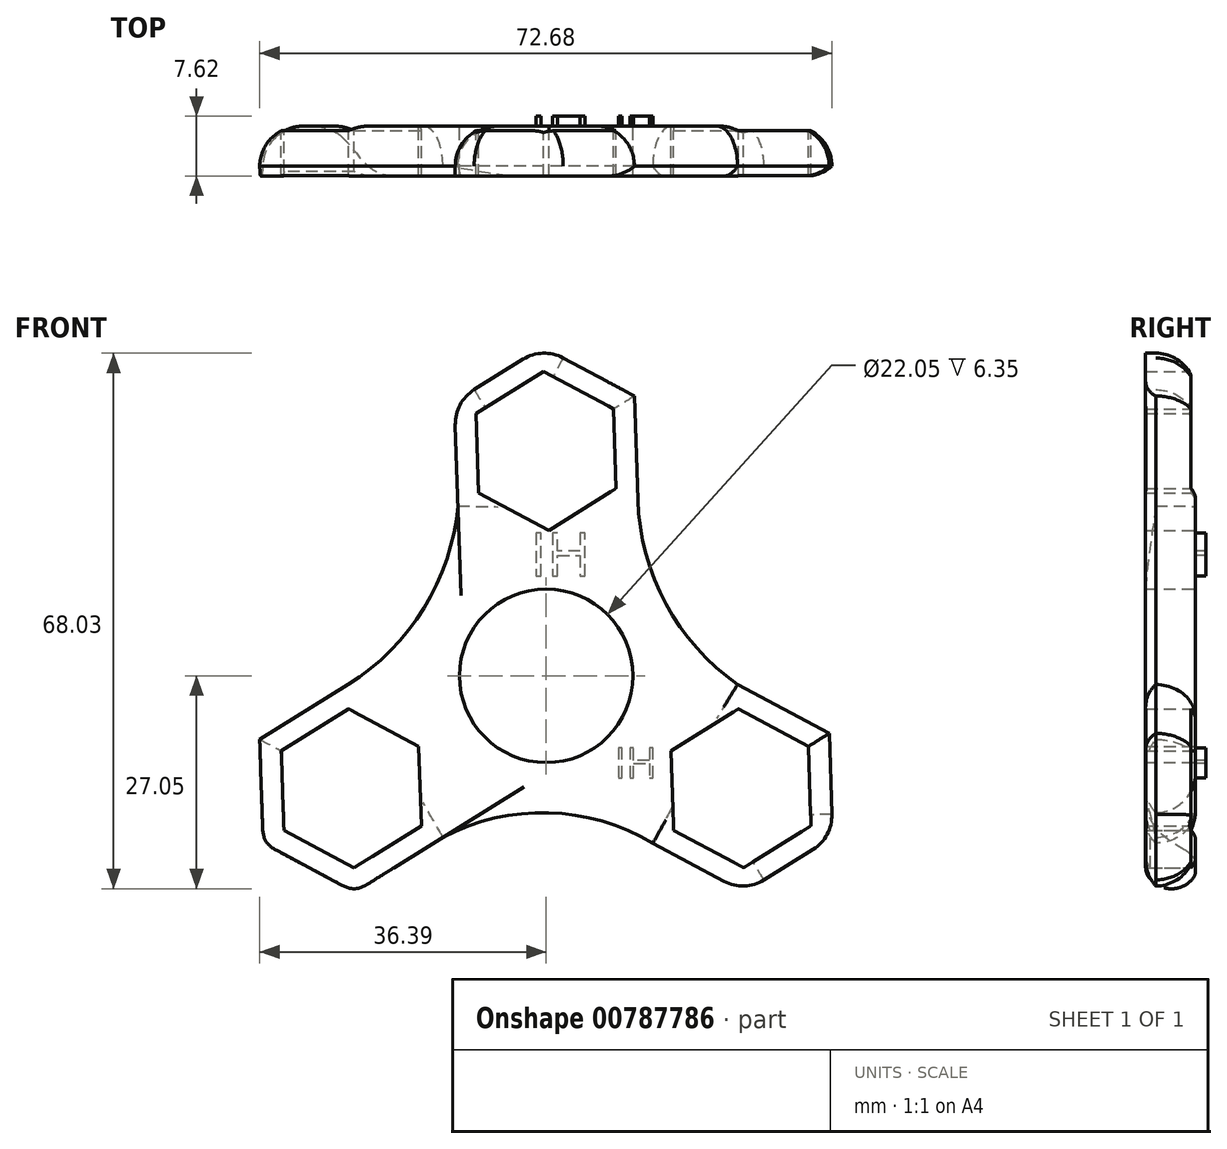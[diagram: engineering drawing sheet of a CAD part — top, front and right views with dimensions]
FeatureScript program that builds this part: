
annotation { "Feature Type Name" : "Feature", "Feature Type Description" : "" }
export const myFeature = defineFeature(function(context is Context, id is Id, definition is map)
    precondition{}
    {
        {
            var Q0;
            Q0=qCreatedBy(makeId("Front.planeOp"),FACE);
            var sketch = newSketch(context, id + "F0", { "sketchPlane" : qUnion([Q0])});
            skCircle(sketch, "E0", {"center": v(0, 0) * mm, "radius": 11.02 * mm});
            skCircle(sketch, "E1", {"center": v(0, 0) * mm, "radius": 14.29 * mm});
            skCircle(sketch, "E2", {"center": v(0, 28.58) * mm, "radius": 8.74 * mm});
            skCircle(sketch, "E3", {"center": v(0, 28.58) * mm, "radius": 11.43 * mm});
            skCircle(sketch, "E4.cCircle", {"center": v(0, 28.58) * mm, "radius": 8.74 * mm, "construction": true});
            skLineSegment(sketch, "E4.0", {"start": v(0.33, 18.5) * mm, "end": v(-8.57, 23.25) * mm});
            skLineSegment(sketch, "E4.1", {"start": v(-8.57, 23.25) * mm, "end": v(-8.9, 33.33) * mm});
            skLineSegment(sketch, "E4.2", {"start": v(-8.9, 33.33) * mm, "end": v(-0.33, 38.66) * mm});
            skLineSegment(sketch, "E4.3", {"start": v(-0.33, 38.66) * mm, "end": v(8.57, 33.9) * mm});
            skLineSegment(sketch, "E4.4", {"start": v(8.57, 33.9) * mm, "end": v(8.9, 23.82) * mm});
            skLineSegment(sketch, "E4.5", {"start": v(8.9, 23.82) * mm, "end": v(0.33, 18.5) * mm});
            skPoint(sketch, "E4.0.midPoint", {"position": v(-4.12, 20.87) * mm});
            skCircle(sketch, "E5.cCircle", {"center": v(0, 28.58) * mm, "radius": 11.43 * mm, "construction": true});
            skLineSegment(sketch, "E5.0", {"start": v(0.43, 15.38) * mm, "end": v(-11.2, 21.6) * mm});
            skLineSegment(sketch, "E5.1", {"start": v(-11.2, 21.6) * mm, "end": v(-11.64, 34.8) * mm});
            skLineSegment(sketch, "E5.2", {"start": v(-11.64, 34.8) * mm, "end": v(-0.43, 41.77) * mm});
            skLineSegment(sketch, "E5.3", {"start": v(-0.43, 41.77) * mm, "end": v(11.2, 35.55) * mm});
            skLineSegment(sketch, "E5.4", {"start": v(11.2, 35.55) * mm, "end": v(11.64, 22.36) * mm});
            skLineSegment(sketch, "E5.5", {"start": v(11.64, 22.36) * mm, "end": v(0.43, 15.38) * mm});
            skPoint(sketch, "E5.0.midPoint", {"position": v(-5.39, 18.5) * mm});
            skCircle(sketch, "E6.1.0", {"center": v(-24.75, -14.29) * mm, "radius": 8.74 * mm, "construction": true});
            skPoint(sketch, "E6.1.1", {"position": v(-16.01, -14) * mm});
            skPoint(sketch, "E6.1.2", {"position": v(-13.32, -13.91) * mm});
            skLineSegment(sketch, "E6.1.3", {"start": v(-35.95, -21.26) * mm, "end": v(-36.39, -8.07) * mm});
            skLineSegment(sketch, "E6.1.4", {"start": v(-24.31, -27.48) * mm, "end": v(-35.95, -21.26) * mm});
            skLineSegment(sketch, "E6.1.5", {"start": v(-13.1, -20.5) * mm, "end": v(-24.31, -27.48) * mm});
            skLineSegment(sketch, "E6.1.6", {"start": v(-25.18, -1.1) * mm, "end": v(-13.54, -7.32) * mm});
            skLineSegment(sketch, "E6.1.7", {"start": v(-15.85, -19.04) * mm, "end": v(-24.42, -24.37) * mm});
            skLineSegment(sketch, "E6.1.8", {"start": v(-24.42, -24.37) * mm, "end": v(-33.31, -19.62) * mm});
            skLineSegment(sketch, "E6.1.9", {"start": v(-33.65, -9.53) * mm, "end": v(-25.08, -4.2) * mm});
            skLineSegment(sketch, "E6.1.10", {"start": v(-25.08, -4.2) * mm, "end": v(-16.18, -8.96) * mm});
            skCircle(sketch, "E6.1.11", {"center": v(-24.75, -14.29) * mm, "radius": 11.43 * mm, "construction": true});
            skLineSegment(sketch, "E6.1.12", {"start": v(-36.39, -8.07) * mm, "end": v(-25.18, -1.1) * mm});
            skCircle(sketch, "E6.1.13", {"center": v(-24.75, -14.29) * mm, "radius": 8.74 * mm});
            skCircle(sketch, "E6.1.14", {"center": v(-24.75, -14.29) * mm, "radius": 11.43 * mm});
            skLineSegment(sketch, "E6.1.15", {"start": v(-16.18, -8.96) * mm, "end": v(-15.85, -19.04) * mm});
            skLineSegment(sketch, "E6.1.16", {"start": v(-33.31, -19.62) * mm, "end": v(-33.65, -9.53) * mm});
            skLineSegment(sketch, "E6.1.17", {"start": v(-13.54, -7.32) * mm, "end": v(-13.1, -20.5) * mm});
            skCircle(sketch, "E6.2.0", {"center": v(24.75, -14.29) * mm, "radius": 8.74 * mm, "construction": true});
            skPoint(sketch, "E6.2.1", {"position": v(20.13, -6.87) * mm});
            skPoint(sketch, "E6.2.2", {"position": v(18.7, -4.58) * mm});
            skLineSegment(sketch, "E6.2.3", {"start": v(36.39, -20.5) * mm, "end": v(25.18, -27.48) * mm});
            skLineSegment(sketch, "E6.2.4", {"start": v(35.95, -7.32) * mm, "end": v(36.39, -20.5) * mm});
            skLineSegment(sketch, "E6.2.5", {"start": v(24.31, -1.1) * mm, "end": v(35.95, -7.32) * mm});
            skLineSegment(sketch, "E6.2.6", {"start": v(13.54, -21.26) * mm, "end": v(13.1, -8.07) * mm});
            skLineSegment(sketch, "E6.2.7", {"start": v(24.42, -4.2) * mm, "end": v(33.31, -8.96) * mm});
            skLineSegment(sketch, "E6.2.8", {"start": v(33.31, -8.96) * mm, "end": v(33.65, -19.04) * mm});
            skLineSegment(sketch, "E6.2.9", {"start": v(25.08, -24.37) * mm, "end": v(16.18, -19.62) * mm});
            skLineSegment(sketch, "E6.2.10", {"start": v(16.18, -19.62) * mm, "end": v(15.85, -9.53) * mm});
            skCircle(sketch, "E6.2.11", {"center": v(24.75, -14.29) * mm, "radius": 11.43 * mm, "construction": true});
            skLineSegment(sketch, "E6.2.12", {"start": v(25.18, -27.48) * mm, "end": v(13.54, -21.26) * mm});
            skCircle(sketch, "E6.2.13", {"center": v(24.75, -14.29) * mm, "radius": 8.74 * mm});
            skCircle(sketch, "E6.2.14", {"center": v(24.75, -14.29) * mm, "radius": 11.43 * mm});
            skLineSegment(sketch, "E6.2.15", {"start": v(15.85, -9.53) * mm, "end": v(24.42, -4.2) * mm});
            skLineSegment(sketch, "E6.2.16", {"start": v(33.65, -19.04) * mm, "end": v(25.08, -24.37) * mm});
            skLineSegment(sketch, "E6.2.17", {"start": v(13.1, -8.07) * mm, "end": v(24.31, -1.1) * mm});
            skArc(sketch, "E7", {"start": v(-25.18, -1.1) * mm, "mid": v(-15.52, 8.6) * mm, "end": v(-11.2, 21.6) * mm});
            skArc(sketch, "E8", {"start": v(11.64, 22.36) * mm, "mid": v(15.22, 9.14) * mm, "end": v(24.31, -1.1) * mm});
            skArc(sketch, "E9", {"start": v(13.54, -21.26) * mm, "mid": v(0.32, -17.4) * mm, "end": v(-13.1, -20.5) * mm});
            skSolve(sketch);
        }
        {
            var Q0;
            {var subQ0=sQuery(id+"F0.wireOp",EDGE,"E5.2");var subQ1=sQuery(id+"F0.wireOp",EDGE,"E3");var subQ2=makeQuery(id+"F0.imprint","INTERSECT",VERTEX,{"derivedFrom":[subQ1,subQ0]});Q0=makeQuery(id+"F0.imprint","IMPRINT",FACE,{"disambiguationData":[TD([[makeQuery(id+"F0.imprint","IMPRINT",EDGE,{"disambiguationData":[TD([[subQ2,-1.0]])],"derivedFrom":subQ1}),-1.0]])]});}
            var Q1;
            {var subQ0=sQuery(id+"F0.wireOp",EDGE,"E5.3");var subQ1=sQuery(id+"F0.wireOp",EDGE,"E3");var subQ2=makeQuery(id+"F0.imprint","INTERSECT",VERTEX,{"derivedFrom":[subQ1,subQ0]});Q1=makeQuery(id+"F0.imprint","IMPRINT",FACE,{"disambiguationData":[TD([[makeQuery(id+"F0.imprint","IMPRINT",EDGE,{"disambiguationData":[TD([[subQ2,-1.0]])],"derivedFrom":subQ1}),-1.0]])]});}
            var Q2;
            {var subQ10=sQuery(id+"F0.wireOp",EDGE,"E3");var subQ14=makeQuery(id+"F0.imprint","INTERSECT",VERTEX,{"derivedFrom":[subQ10,sQuery(id+"F0.wireOp",EDGE,"E5.3")]});Q2=makeQuery(id+"F0.imprint","IMPRINT",FACE,{"disambiguationData":[TD([[makeQuery(id+"F0.imprint","IMPRINT",EDGE,{"disambiguationData":[TD([[subQ14,1.0]])],"derivedFrom":subQ10}),1.0]])]});}
            var Q3;
            {var subQ0=sQuery(id+"F0.wireOp",EDGE,"E5.3");var subQ1=sQuery(id+"F0.wireOp",EDGE,"E3");var subQ2=makeQuery(id+"F0.imprint","INTERSECT",VERTEX,{"derivedFrom":[subQ1,subQ0]});Q3=makeQuery(id+"F0.imprint","IMPRINT",FACE,{"disambiguationData":[TD([[makeQuery(id+"F0.imprint","IMPRINT",EDGE,{"disambiguationData":[TD([[subQ2,1.0]])],"derivedFrom":subQ1}),-1.0]])]});}
            var Q4;
            {var subQ0=sQuery(id+"F0.wireOp",EDGE,"E5.4");var subQ1=sQuery(id+"F0.wireOp",EDGE,"E3");var subQ2=makeQuery(id+"F0.imprint","INTERSECT",VERTEX,{"derivedFrom":[subQ1,subQ0]});Q4=makeQuery(id+"F0.imprint","IMPRINT",FACE,{"disambiguationData":[TD([[makeQuery(id+"F0.imprint","IMPRINT",EDGE,{"disambiguationData":[TD([[subQ2,1.0]])],"derivedFrom":subQ1}),-1.0]])]});}
            var Q5;
            {var subQ0=sQuery(id+"F0.wireOp",EDGE,"E5.0");var subQ1=sQuery(id+"F0.wireOp",EDGE,"E3");var subQ2=makeQuery(id+"F0.imprint","INTERSECT",VERTEX,{"derivedFrom":[subQ1,subQ0]});Q5=makeQuery(id+"F0.imprint","IMPRINT",FACE,{"disambiguationData":[TD([[makeQuery(id+"F0.imprint","IMPRINT",EDGE,{"disambiguationData":[TD([[subQ2,-1.0]])],"derivedFrom":subQ1}),-1.0]])]});}
            var Q6;
            {var subQ0=sQuery(id+"F0.wireOp",EDGE,"E5.1");var subQ1=sQuery(id+"F0.wireOp",EDGE,"E3");var subQ2=makeQuery(id+"F0.imprint","INTERSECT",VERTEX,{"derivedFrom":[subQ1,subQ0]});Q6=makeQuery(id+"F0.imprint","IMPRINT",FACE,{"disambiguationData":[TD([[makeQuery(id+"F0.imprint","IMPRINT",EDGE,{"disambiguationData":[TD([[subQ2,-1.0]])],"derivedFrom":subQ1}),-1.0]])]});}
            var Q7;
            Q7=makeQuery(id+"F0.imprint","IMPRINT",FACE,{"disambiguationData":[TD([[makeQuery(id+"F0.imprint","IMPRINT",EDGE,{"derivedFrom":sQuery(id+"F0.wireOp",EDGE,"E1")}),-1.0]])]});
            var Q8;
            Q8=makeQuery(id+"F0.imprint","IMPRINT",FACE,{"disambiguationData":[TD([[makeQuery(id+"F0.imprint","IMPRINT",EDGE,{"derivedFrom":sQuery(id+"F0.wireOp",EDGE,"E0")}),-1.0]])]});
            var Q9;
            {var subQ1=sQuery(id+"F0.wireOp",EDGE,"E6.2.5");var subQ3=sQuery(id+"F0.wireOp",EDGE,"E6.2.14");var subQ4=makeQuery(id+"F0.imprint","INTERSECT",VERTEX,{"derivedFrom":[subQ1,subQ3]});Q9=makeQuery(id+"F0.imprint","IMPRINT",FACE,{"disambiguationData":[TD([[makeQuery(id+"F0.imprint","IMPRINT",EDGE,{"disambiguationData":[TD([[subQ4,-1.0]])],"derivedFrom":subQ3}),-1.0]])]});}
            var Q10;
            {var subQ1=sQuery(id+"F0.wireOp",EDGE,"E6.1.5");var subQ3=sQuery(id+"F0.wireOp",EDGE,"E6.1.14");var subQ4=makeQuery(id+"F0.imprint","INTERSECT",VERTEX,{"derivedFrom":[subQ1,subQ3]});Q10=makeQuery(id+"F0.imprint","IMPRINT",FACE,{"disambiguationData":[TD([[makeQuery(id+"F0.imprint","IMPRINT",EDGE,{"disambiguationData":[TD([[subQ4,-1.0]])],"derivedFrom":subQ3}),-1.0]])]});}
            var Q11;
            {var subQ0=sQuery(id+"F0.wireOp",EDGE,"E6.1.17");var subQ1=sQuery(id+"F0.wireOp",EDGE,"E6.1.6");var subQ2=makeQuery(id+"F0.imprint","INTERSECT",VERTEX,{"derivedFrom":[subQ1,subQ0]});Q11=makeQuery(id+"F0.imprint","IMPRINT",FACE,{"disambiguationData":[TD([[makeQuery(id+"F0.imprint","IMPRINT",EDGE,{"disambiguationData":[TD([[subQ2,1.0]])],"derivedFrom":subQ1}),-1.0]])]});}
            var Q12;
            {var subQ0=sQuery(id+"F0.wireOp",EDGE,"E6.1.12");var subQ3=sQuery(id+"F0.wireOp",EDGE,"E6.1.14");var subQ5=makeQuery(id+"F0.imprint","INTERSECT",VERTEX,{"derivedFrom":[subQ0,subQ3]});Q12=makeQuery(id+"F0.imprint","IMPRINT",FACE,{"disambiguationData":[TD([[makeQuery(id+"F0.imprint","IMPRINT",EDGE,{"disambiguationData":[TD([[subQ5,1.0]])],"derivedFrom":subQ3}),-1.0]])]});}
            var Q13;
            {var subQ0=sQuery(id+"F0.wireOp",EDGE,"E6.1.15");var subQ14=sQuery(id+"F0.wireOp",EDGE,"E6.1.7");var subQ15=makeQuery(id+"F0.imprint","INTERSECT",VERTEX,{"derivedFrom":[subQ14,subQ0]});Q13=makeQuery(id+"F0.imprint","IMPRINT",FACE,{"disambiguationData":[TD([[makeQuery(id+"F0.imprint","IMPRINT",EDGE,{"disambiguationData":[TD([[subQ15,-1.0]])],"derivedFrom":subQ14}),1.0]])]});}
            var Q14;
            {var subQ0=sQuery(id+"F0.wireOp",EDGE,"E6.1.12");var subQ1=sQuery(id+"F0.wireOp",EDGE,"E6.1.3");var subQ2=makeQuery(id+"F0.imprint","INTERSECT",VERTEX,{"derivedFrom":[subQ1,subQ0]});Q14=makeQuery(id+"F0.imprint","IMPRINT",FACE,{"disambiguationData":[TD([[makeQuery(id+"F0.imprint","IMPRINT",EDGE,{"disambiguationData":[TD([[subQ2,1.0]])],"derivedFrom":subQ1}),-1.0]])]});}
            var Q15;
            {var subQ0=sQuery(id+"F0.wireOp",EDGE,"E6.1.4");var subQ1=sQuery(id+"F0.wireOp",EDGE,"E6.1.3");var subQ2=makeQuery(id+"F0.imprint","INTERSECT",VERTEX,{"derivedFrom":[subQ1,subQ0]});Q15=makeQuery(id+"F0.imprint","IMPRINT",FACE,{"disambiguationData":[TD([[makeQuery(id+"F0.imprint","IMPRINT",EDGE,{"disambiguationData":[TD([[subQ2,-1.0]])],"derivedFrom":subQ1}),-1.0]])]});}
            var Q16;
            {var subQ0=sQuery(id+"F0.wireOp",EDGE,"E6.1.5");var subQ1=sQuery(id+"F0.wireOp",EDGE,"E6.1.4");var subQ2=makeQuery(id+"F0.imprint","INTERSECT",VERTEX,{"derivedFrom":[subQ1,subQ0]});Q16=makeQuery(id+"F0.imprint","IMPRINT",FACE,{"disambiguationData":[TD([[makeQuery(id+"F0.imprint","IMPRINT",EDGE,{"disambiguationData":[TD([[subQ2,-1.0]])],"derivedFrom":subQ1}),-1.0]])]});}
            var Q17;
            {var subQ0=sQuery(id+"F0.wireOp",EDGE,"E6.2.17");var subQ1=sQuery(id+"F0.wireOp",EDGE,"E6.2.6");var subQ2=makeQuery(id+"F0.imprint","INTERSECT",VERTEX,{"derivedFrom":[subQ1,subQ0]});Q17=makeQuery(id+"F0.imprint","IMPRINT",FACE,{"disambiguationData":[TD([[makeQuery(id+"F0.imprint","IMPRINT",EDGE,{"disambiguationData":[TD([[subQ2,1.0]])],"derivedFrom":subQ1}),-1.0]])]});}
            var Q18;
            {var subQ0=sQuery(id+"F0.wireOp",EDGE,"E6.2.12");var subQ3=sQuery(id+"F0.wireOp",EDGE,"E6.2.14");var subQ5=makeQuery(id+"F0.imprint","INTERSECT",VERTEX,{"derivedFrom":[subQ0,subQ3]});Q18=makeQuery(id+"F0.imprint","IMPRINT",FACE,{"disambiguationData":[TD([[makeQuery(id+"F0.imprint","IMPRINT",EDGE,{"disambiguationData":[TD([[subQ5,1.0]])],"derivedFrom":subQ3}),-1.0]])]});}
            var Q19;
            {var subQ0=sQuery(id+"F0.wireOp",EDGE,"E6.2.12");var subQ1=sQuery(id+"F0.wireOp",EDGE,"E6.2.3");var subQ2=makeQuery(id+"F0.imprint","INTERSECT",VERTEX,{"derivedFrom":[subQ1,subQ0]});Q19=makeQuery(id+"F0.imprint","IMPRINT",FACE,{"disambiguationData":[TD([[makeQuery(id+"F0.imprint","IMPRINT",EDGE,{"disambiguationData":[TD([[subQ2,1.0]])],"derivedFrom":subQ1}),-1.0]])]});}
            var Q20;
            {var subQ0=sQuery(id+"F0.wireOp",EDGE,"E6.2.4");var subQ1=sQuery(id+"F0.wireOp",EDGE,"E6.2.3");var subQ2=makeQuery(id+"F0.imprint","INTERSECT",VERTEX,{"derivedFrom":[subQ1,subQ0]});Q20=makeQuery(id+"F0.imprint","IMPRINT",FACE,{"disambiguationData":[TD([[makeQuery(id+"F0.imprint","IMPRINT",EDGE,{"disambiguationData":[TD([[subQ2,-1.0]])],"derivedFrom":subQ1}),-1.0]])]});}
            var Q21;
            {var subQ0=sQuery(id+"F0.wireOp",EDGE,"E6.2.5");var subQ1=sQuery(id+"F0.wireOp",EDGE,"E6.2.4");var subQ2=makeQuery(id+"F0.imprint","INTERSECT",VERTEX,{"derivedFrom":[subQ1,subQ0]});Q21=makeQuery(id+"F0.imprint","IMPRINT",FACE,{"disambiguationData":[TD([[makeQuery(id+"F0.imprint","IMPRINT",EDGE,{"disambiguationData":[TD([[subQ2,-1.0]])],"derivedFrom":subQ1}),-1.0]])]});}
            var Q22;
            {var subQ0=sQuery(id+"F0.wireOp",EDGE,"E6.2.15");var subQ14=sQuery(id+"F0.wireOp",EDGE,"E6.2.7");var subQ15=makeQuery(id+"F0.imprint","INTERSECT",VERTEX,{"derivedFrom":[subQ14,subQ0]});Q22=makeQuery(id+"F0.imprint","IMPRINT",FACE,{"disambiguationData":[TD([[makeQuery(id+"F0.imprint","IMPRINT",EDGE,{"disambiguationData":[TD([[subQ15,-1.0]])],"derivedFrom":subQ14}),1.0]])]});}
            extrude(context, id + "F1", {"entities" : qUnion([Q0, Q1, Q2, Q3, Q4, Q5, Q6, Q7, Q8, Q9, Q10, Q11, Q12, Q13, Q14, Q15, Q16, Q17, Q18, Q19, Q20, Q21, Q22]), "depth" : 6.35 * mm, "offsetDistance" : 25.4 * mm});
        }
        {
            var Q0;
            Q0=makeQuery(id+"F1.opExtrude","CAP_EDGE",EDGE,{"disambiguationData":[OSD([sQuery(id+"F0.wireOp",EDGE,"E5.3")])],"isStart":true});
            var Q1;
            Q1=makeQuery(id+"F1.opExtrude","CAP_EDGE",EDGE,{"disambiguationData":[OSD([sQuery(id+"F0.wireOp",EDGE,"E5.4")])],"isStart":true});
            fillet(context, id + "F2", {"entities" : qUnion([Q0, Q1]), "radius" : 5.08 * mm, "tangentPropagation" : true, "allowEdgeOverflow" : false});
        }
        {
            var Q0;
            Q0=makeQuery(id+"F1.opExtrude","CAP_EDGE",EDGE,{"disambiguationData":[OSD([sQuery(id+"F0.wireOp",EDGE,"E5.2")])],"isStart":true});
            fillet(context, id + "F3", {"entities" : qUnion([Q0]), "radius" : 5.08 * mm, "tangentPropagation" : true, "allowEdgeOverflow" : false});
        }
        {
            var Q0;
            Q0=makeQuery(id+"F1.opExtrude","CAP_EDGE",EDGE,{"disambiguationData":[OSD([sQuery(id+"F0.wireOp",EDGE,"E6.2.5")])],"isStart":true});
            var Q1;
            Q1=makeQuery(id+"F1.opExtrude","CAP_EDGE",EDGE,{"disambiguationData":[OSD([sQuery(id+"F0.wireOp",EDGE,"E6.2.4")])],"isStart":true});
            fillet(context, id + "F4", {"entities" : qUnion([Q0, Q1]), "radius" : 5.08 * mm, "tangentPropagation" : true, "allowEdgeOverflow" : false});
        }
        {
            var Q0;
            Q0=makeQuery(id+"F4.opFillet","BLEND_EDGE",EDGE,{"blendedFrom":[makeQuery(id+"F1.opExtrude","CAP_EDGE",EDGE,{"disambiguationData":[OSD([sQuery(id+"F0.wireOp",EDGE,"E6.2.4")])],"isStart":true}),makeQuery(id+"F1.opExtrude","SWEPT_FACE",FACE,{"disambiguationData":[OSD([sQuery(id+"F0.wireOp",EDGE,"E6.2.3")])]})],"blendedInto":[makeQuery(id+"F1.opExtrude","SWEPT_FACE",FACE,{"disambiguationData":[OSD([sQuery(id+"F0.wireOp",EDGE,"E6.2.3")])]})]});
            var Q1;
            Q1=makeQuery(id+"F1.opExtrude","CAP_EDGE",EDGE,{"disambiguationData":[OSD([sQuery(id+"F0.wireOp",EDGE,"E6.2.3")])],"isStart":true});
            fillet(context, id + "F5", {"entities" : qUnion([Q0, Q1]), "radius" : 5.08 * mm, "tangentPropagation" : true, "allowEdgeOverflow" : false});
        }
        {
            var Q0;
            Q0=makeQuery(id+"F1.opExtrude","CAP_EDGE",EDGE,{"disambiguationData":[OSD([sQuery(id+"F0.wireOp",EDGE,"E6.2.12")])],"isStart":true});
            fillet(context, id + "F6", {"entities" : qUnion([Q0]), "radius" : 5.08 * mm, "tangentPropagation" : true, "allowEdgeOverflow" : false});
        }
        {
            var Q0;
            Q0=makeQuery(id+"F1.opExtrude","CAP_EDGE",EDGE,{"disambiguationData":[OSD([sQuery(id+"F0.wireOp",EDGE,"E6.1.3")])],"isStart":true});
            var Q1;
            Q1=makeQuery(id+"F1.opExtrude","CAP_EDGE",EDGE,{"disambiguationData":[OSD([sQuery(id+"F0.wireOp",EDGE,"E6.1.12")])],"isStart":true});
            var Q2;
            Q2=makeQuery(id+"F1.opExtrude","CAP_EDGE",EDGE,{"disambiguationData":[OSD([sQuery(id+"F0.wireOp",EDGE,"E5.1")])],"isStart":true});
            fillet(context, id + "F7", {"entities" : qUnion([Q0, Q1, Q2]), "radius" : 5.08 * mm, "tangentPropagation" : true, "allowEdgeOverflow" : false});
        }
        {
            var Q0;
            Q0=qCreatedBy(makeId("Front.planeOp"),FACE);
            var sketch = newSketch(context, id + "F8", { "sketchPlane" : qUnion([Q0])});
            skCircle(sketch, "E10", {"center": v(6.13, 15.17) * mm, "radius": 2.03 * mm});
            skCircle(sketch, "E11", {"center": v(-3.97, 15.75) * mm, "radius": 2.34 * mm});
            skSolve(sketch);
        }
        {
            var Q0;
            Q0=makeQuery(id+"F8.imprint","IMPRINT",FACE,{"disambiguationData":[TD([[makeQuery(id+"F8.imprint","IMPRINT",EDGE,{"derivedFrom":sQuery(id+"F8.wireOp",EDGE,"E11")}),1.0]])]});
            var Q1;
            Q1=makeQuery(id+"F8.imprint","IMPRINT",FACE,{"disambiguationData":[TD([[makeQuery(id+"F8.imprint","IMPRINT",EDGE,{"derivedFrom":sQuery(id+"F8.wireOp",EDGE,"E10")}),1.0]])]});
            extrude(context, id + "F9", {"entities" : qUnion([Q0, Q1]), "operationType" : NewBodyOperationType.REMOVE, "oppositeDirection" : true, "depth" : 1.27 * mm, "offsetDistance" : 25.4 * mm});
        }
        {
            var Q0;
            Q0=makeQuery(id+"F7.opFillet","SPLIT",FACE,{"disambiguationData":[OD(1.0)],"derivedFrom":makeQuery(id+"F1.opExtrude","CAP_FACE",FACE,{"disambiguationData":[OSD([sQuery(id+"F0.wireOp",EDGE,"E0"),sQuery(id+"F0.wireOp",EDGE,"E4.0"),sQuery(id+"F0.wireOp",EDGE,"E4.1"),sQuery(id+"F0.wireOp",EDGE,"E4.2"),sQuery(id+"F0.wireOp",EDGE,"E4.3"),sQuery(id+"F0.wireOp",EDGE,"E4.4"),sQuery(id+"F0.wireOp",EDGE,"E4.5"),sQuery(id+"F0.wireOp",EDGE,"E5.1"),sQuery(id+"F0.wireOp",EDGE,"E5.2"),sQuery(id+"F0.wireOp",EDGE,"E5.3"),sQuery(id+"F0.wireOp",EDGE,"E5.4"),sQuery(id+"F0.wireOp",EDGE,"E6.1.3"),sQuery(id+"F0.wireOp",EDGE,"E6.1.4"),sQuery(id+"F0.wireOp",EDGE,"E6.1.5"),sQuery(id+"F0.wireOp",EDGE,"E6.1.7"),sQuery(id+"F0.wireOp",EDGE,"E6.1.8"),sQuery(id+"F0.wireOp",EDGE,"E6.1.9"),sQuery(id+"F0.wireOp",EDGE,"E6.1.10"),sQuery(id+"F0.wireOp",EDGE,"E6.1.12"),sQuery(id+"F0.wireOp",EDGE,"E6.1.15"),sQuery(id+"F0.wireOp",EDGE,"E6.1.16"),sQuery(id+"F0.wireOp",EDGE,"E6.2.3"),sQuery(id+"F0.wireOp",EDGE,"E6.2.4"),sQuery(id+"F0.wireOp",EDGE,"E6.2.5"),sQuery(id+"F0.wireOp",EDGE,"E6.2.7"),sQuery(id+"F0.wireOp",EDGE,"E6.2.8"),sQuery(id+"F0.wireOp",EDGE,"E6.2.9"),sQuery(id+"F0.wireOp",EDGE,"E6.2.10"),sQuery(id+"F0.wireOp",EDGE,"E6.2.12"),sQuery(id+"F0.wireOp",EDGE,"E6.2.15"),sQuery(id+"F0.wireOp",EDGE,"E6.2.16"),sQuery(id+"F0.wireOp",EDGE,"E7"),sQuery(id+"F0.wireOp",EDGE,"E8"),sQuery(id+"F0.wireOp",EDGE,"E9")])],"isStart":true})});
            var sketch = newSketch(context, id + "F10", { "sketchPlane" : qUnion([Q0])});
            skText(sketch, "E12", { "text": "HI", "fontName": "OpenSans-Regular.ttf"});
            const initialGuessF10  = {"E12": [-0.00571, 0.0127, 1, 0, 0.0055]};
            skSetInitialGuess(sketch, initialGuessF10);
            skSolve(sketch);
        }
        {
            var Q0;
            Q0 = qSketchRegion(id + "F10", true);
            extrude(context, id + "F11", {"entities" : qUnion([Q0]), "operationType" : NewBodyOperationType.ADD, "depth" : 1.27 * mm, "offsetDistance" : 25.4 * mm});
        }
        {
            var Q0;
            Q0=makeQuery(id+"F7.opFillet","SPLIT",FACE,{"disambiguationData":[OD(1.0)],"derivedFrom":makeQuery(id+"F1.opExtrude","CAP_FACE",FACE,{"disambiguationData":[OSD([sQuery(id+"F0.wireOp",EDGE,"E0"),sQuery(id+"F0.wireOp",EDGE,"E4.0"),sQuery(id+"F0.wireOp",EDGE,"E4.1"),sQuery(id+"F0.wireOp",EDGE,"E4.2"),sQuery(id+"F0.wireOp",EDGE,"E4.3"),sQuery(id+"F0.wireOp",EDGE,"E4.4"),sQuery(id+"F0.wireOp",EDGE,"E4.5"),sQuery(id+"F0.wireOp",EDGE,"E5.1"),sQuery(id+"F0.wireOp",EDGE,"E5.2"),sQuery(id+"F0.wireOp",EDGE,"E5.3"),sQuery(id+"F0.wireOp",EDGE,"E5.4"),sQuery(id+"F0.wireOp",EDGE,"E6.1.3"),sQuery(id+"F0.wireOp",EDGE,"E6.1.4"),sQuery(id+"F0.wireOp",EDGE,"E6.1.5"),sQuery(id+"F0.wireOp",EDGE,"E6.1.7"),sQuery(id+"F0.wireOp",EDGE,"E6.1.8"),sQuery(id+"F0.wireOp",EDGE,"E6.1.9"),sQuery(id+"F0.wireOp",EDGE,"E6.1.10"),sQuery(id+"F0.wireOp",EDGE,"E6.1.12"),sQuery(id+"F0.wireOp",EDGE,"E6.1.15"),sQuery(id+"F0.wireOp",EDGE,"E6.1.16"),sQuery(id+"F0.wireOp",EDGE,"E6.2.3"),sQuery(id+"F0.wireOp",EDGE,"E6.2.4"),sQuery(id+"F0.wireOp",EDGE,"E6.2.5"),sQuery(id+"F0.wireOp",EDGE,"E6.2.7"),sQuery(id+"F0.wireOp",EDGE,"E6.2.8"),sQuery(id+"F0.wireOp",EDGE,"E6.2.9"),sQuery(id+"F0.wireOp",EDGE,"E6.2.10"),sQuery(id+"F0.wireOp",EDGE,"E6.2.12"),sQuery(id+"F0.wireOp",EDGE,"E6.2.15"),sQuery(id+"F0.wireOp",EDGE,"E6.2.16"),sQuery(id+"F0.wireOp",EDGE,"E7"),sQuery(id+"F0.wireOp",EDGE,"E8"),sQuery(id+"F0.wireOp",EDGE,"E9")])],"isStart":true})});
            var sketch = newSketch(context, id + "F12", { "sketchPlane" : qUnion([Q0])});
            skText(sketch, "E13", { "text": "HI", "fontName": "OpenSans-Regular.ttf"});
            const initialGuessF12  = {"E13": [-0.01407, -0.01294, 1, 0, 0.00384]};
            skSetInitialGuess(sketch, initialGuessF12);
            skSolve(sketch);
        }
        {
            var Q0;
            Q0 = qSketchRegion(id + "F12", true);
            extrude(context, id + "F13", {"entities" : qUnion([Q0]), "operationType" : NewBodyOperationType.ADD, "depth" : 1.27 * mm, "offsetDistance" : 25.4 * mm});
        }
        {
            var Q0;
            Q0=makeQuery(id+"F1.opExtrude","CAP_EDGE",EDGE,{"disambiguationData":[OSD([sQuery(id+"F0.wireOp",EDGE,"E5.4")])],"isStart":false});
            var Q1;
            Q1=makeQuery(id+"F1.opExtrude","CAP_EDGE",EDGE,{"disambiguationData":[OSD([sQuery(id+"F0.wireOp",EDGE,"E6.2.5")])],"isStart":false});
            var Q2;
            Q2=makeQuery(id+"F1.opExtrude","CAP_EDGE",EDGE,{"disambiguationData":[OSD([sQuery(id+"F0.wireOp",EDGE,"E6.2.4")])],"isStart":false});
            fillet(context, id + "F14", {"entities" : qUnion([Q0, Q1, Q2]), "radius" : 5.08 * mm, "tangentPropagation" : true, "allowEdgeOverflow" : false});
        }
        {
            var Q0;
            Q0=makeQuery(id+"F1.opExtrude","CAP_EDGE",EDGE,{"disambiguationData":[OSD([sQuery(id+"F0.wireOp",EDGE,"E6.1.4")])],"isStart":false});
            fillet(context, id + "F15", {"entities" : qUnion([Q0]), "radius" : 5.08 * mm, "tangentPropagation" : true, "allowEdgeOverflow" : false});
        }
        {
            var Q0;
            Q0=makeQuery(id+"F1.opExtrude","CAP_EDGE",EDGE,{"disambiguationData":[OSD([sQuery(id+"F0.wireOp",EDGE,"E7")])],"isStart":false});
            var Q1;
            Q1=makeQuery(id+"F1.opExtrude","CAP_EDGE",EDGE,{"disambiguationData":[OSD([sQuery(id+"F0.wireOp",EDGE,"E6.1.12")])],"isStart":false});
            fillet(context, id + "F16", {"entities" : qUnion([Q0, Q1]), "radius" : 5.08 * mm, "tangentPropagation" : true, "allowEdgeOverflow" : false});
        }
        {
            var Q0;
            Q0=makeQuery(id+"F1.opExtrude","CAP_EDGE",EDGE,{"disambiguationData":[OSD([sQuery(id+"F0.wireOp",EDGE,"E6.1.5")])],"isStart":true});
            fillet(context, id + "F17", {"entities" : qUnion([Q0]), "radius" : 5.08 * mm, "tangentPropagation" : true, "allowEdgeOverflow" : false});
        }
    });
